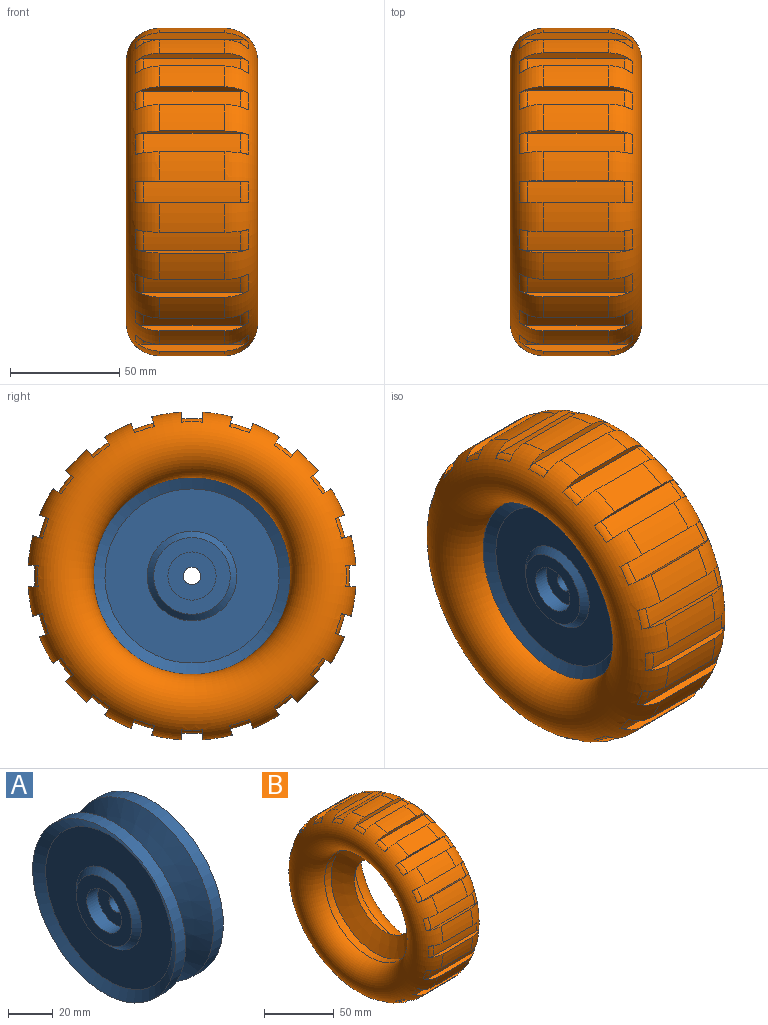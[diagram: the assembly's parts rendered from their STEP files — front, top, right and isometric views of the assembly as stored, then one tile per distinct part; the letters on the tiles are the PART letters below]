
ASSEMBLY  parts=2 mates=1
PART A: 17 faces, bbox 30x90x90 mm
  f0: plane 35x35mm, normal (-1,0,0), area 582mm2, adj f1,f16
  f1: cylinder r=11mm len=22mm, axis (-1,0,0), area 483.8mm2, adj f0,f2
  f2: plane 22x22mm, normal (-1,0,0), area 329.9mm2, adj f1,f3
  f3: cylinder r=4mm len=16mm, axis (-1,0,0), area 402.1mm2, adj f2,f4
  f4: plane 22x22mm, normal (1,0,0), area 329.9mm2, adj f3,f5
  f5: cylinder r=11mm len=22mm, axis (-1,0,0), area 483.8mm2, adj f4,f6
  f6: plane 35x35mm, normal (1,0,0), area 582mm2, adj f5,f15
  f7: plane 79.61x79.61mm, normal (1,0,0), area 3657.1mm2, adj f8,f15
  f8: cone r=39.8mm half-angle=60deg, axis (1,0,0), area 1598.5mm2, adj f7,f9
  f9: cylinder r=45mm len=90mm, axis (-1,0,0), area 1792.5mm2, adj f8,f10
  f10: cone r=45mm half-angle=60deg, axis (1,0,0), area 4081mm2, adj f9,f11
  f11: cone r=30mm half-angle=60deg, axis (-1,0,0), area 4081mm2, adj f10,f12
  f12: cylinder r=45mm len=90mm, axis (-1,0,0), area 1792.5mm2, adj f11,f13
  f13: cone r=39.8mm half-angle=60deg, axis (-1,0,0), area 1598.5mm2, adj f12,f14
  f14: plane 79.61x79.61mm, normal (-1,0,0), area 3657.1mm2, adj f13,f16
  f15: cone r=20.5mm half-angle=45deg, axis (-1,0,0), area 506.5mm2, adj f6,f7
  f16: cone r=17.5mm half-angle=45deg, axis (1,0,0), area 506.5mm2, adj f0,f14
PART B: 126 faces, bbox 60x162.4x162.4 mm
  f0: cylinder r=75mm len=30mm, axis (-1,0,0), area 406.6mm2, adj f20,f25,f28,f122
  f1: cylinder r=75mm len=30mm, axis (-1,0,0), area 406.6mm2, adj f20,f25,f117,f123
  f2: cylinder r=75mm len=30mm, axis (-1,0,0), area 406.6mm2, adj f20,f25,f112,f118
  f3: cylinder r=75mm len=30mm, axis (-1,0,0), area 406.6mm2, adj f20,f25,f107,f113
  f4: cylinder r=75mm len=30mm, axis (-1,0,0), area 406.6mm2, adj f20,f25,f102,f108
  f5: cylinder r=75mm len=30mm, axis (-1,0,0), area 406.6mm2, adj f20,f25,f97,f103
  f6: cylinder r=75mm len=30mm, axis (-1,0,0), area 406.6mm2, adj f20,f25,f92,f98
  f7: cylinder r=75mm len=30mm, axis (-1,0,0), area 406.6mm2, adj f20,f25,f87,f93
  f8: cylinder r=75mm len=30mm, axis (-1,0,0), area 406.6mm2, adj f20,f25,f82,f88
  f9: cylinder r=75mm len=30mm, axis (-1,0,0), area 406.6mm2, adj f20,f25,f77,f83
  f10: cylinder r=75mm len=30mm, axis (-1,0,0), area 406.6mm2, adj f20,f25,f72,f78
  f11: cylinder r=75mm len=30mm, axis (-1,0,0), area 406.6mm2, adj f20,f25,f67,f73
  f12: cylinder r=75mm len=30mm, axis (-1,0,0), area 406.6mm2, adj f20,f25,f62,f68
  f13: cylinder r=75mm len=30mm, axis (-1,0,0), area 406.6mm2, adj f20,f25,f57,f63
  f14: cylinder r=75mm len=30mm, axis (-1,0,0), area 406.6mm2, adj f20,f25,f52,f58
  f15: cylinder r=75mm len=30mm, axis (-1,0,0), area 406.6mm2, adj f20,f25,f47,f53
  f16: cylinder r=75mm len=30mm, axis (-1,0,0), area 406.6mm2, adj f20,f25,f42,f48
  f17: cylinder r=75mm len=30mm, axis (-1,0,0), area 406.6mm2, adj f20,f25,f37,f43
  f18: cylinder r=75mm len=30mm, axis (-1,0,0), area 406.6mm2, adj f20,f25,f32,f38
  f19: cylinder r=75mm len=30mm, axis (-1,0,0), area 406.6mm2, adj f20,f25,f27,f33
  f20: torus R=60mm, axis (-1,0,0), area 15426.1mm2, adj f0,f1,f2,f3,f4,f5,f6,f7
  f21: cylinder r=45mm len=90mm, axis (-1,0,0), area 1792.5mm2, adj f20,f22
  f22: cone r=30mm half-angle=60deg, axis (-1,0,0), area 4081mm2, adj f21,f23
  f23: cone r=45mm half-angle=60deg, axis (1,0,0), area 4081mm2, adj f22,f24
  f24: cylinder r=45mm len=90mm, axis (-1,0,0), area 1792.5mm2, adj f23,f25
  f25: torus R=60mm, axis (-1,0,0), area 15426.1mm2, adj f0,f1,f2,f3,f4,f5,f6,f7
  f26: cylinder r=72mm len=44.28mm, axis (1,0,0), area 425.4mm2, adj f27,f28,f29,f30
  f27: plane 51.42x4.49mm, normal (0,-1,0.07), area 127.7mm2, adj f19,f20,f25,f26,f29,f30
  f28: plane 51.42x4.49mm, normal (0,1,0.07), area 127.7mm2, adj f0,f20,f25,f26,f29,f30
  f29: torus R=67mm, axis (1,0,0), area 37.9mm2, adj f20,f26,f27,f28
  f30: torus R=67mm, axis (-1,0,0), area 37.9mm2, adj f25,f26,f27,f28
  f31: cylinder r=72mm len=44.28mm, axis (1,0,0), area 425.4mm2, adj f32,f33,f34,f35
  f32: plane 51.42x4.18mm, normal (0,-0.93,0.37), area 127.7mm2, adj f18,f20,f25,f31,f34,f35
  f33: plane 51.42x4.36mm, normal (0,0.97,-0.24), area 127.7mm2, adj f19,f20,f25,f31,f34,f35
  f34: torus R=67mm, axis (1,0,0), area 37.9mm2, adj f20,f31,f32,f33
  f35: torus R=67mm, axis (-1,0,0), area 37.9mm2, adj f25,f31,f32,f33
  f36: cylinder r=72mm len=44.28mm, axis (1,0,0), area 425.4mm2, adj f37,f38,f39,f40
  f37: plane 51.42x3.46mm, normal (0,-0.77,0.64), area 127.7mm2, adj f17,f20,f25,f36,f39,f40
  f38: plane 51.42x3.81mm, normal (0,0.85,-0.53), area 127.7mm2, adj f18,f20,f25,f36,f39,f40
  f39: torus R=67mm, axis (1,0,0), area 37.9mm2, adj f20,f36,f37,f38
  f40: torus R=67mm, axis (-1,0,0), area 37.9mm2, adj f25,f36,f37,f38
  f41: cylinder r=72mm len=44.28mm, axis (1,0,0), area 425.4mm2, adj f42,f43,f44,f45
  f42: plane 51.42x3.81mm, normal (0,-0.53,0.85), area 127.7mm2, adj f16,f20,f25,f41,f44,f45
  f43: plane 51.42x3.46mm, normal (0,0.64,-0.77), area 127.7mm2, adj f17,f20,f25,f41,f44,f45
  f44: torus R=67mm, axis (1,0,0), area 37.9mm2, adj f20,f41,f42,f43
  f45: torus R=67mm, axis (-1,0,0), area 37.9mm2, adj f25,f41,f42,f43
  f46: cylinder r=72mm len=44.28mm, axis (1,0,0), area 425.4mm2, adj f47,f48,f49,f50
  f47: plane 51.42x4.36mm, normal (0,-0.24,0.97), area 127.7mm2, adj f15,f20,f25,f46,f49,f50
  f48: plane 51.42x4.18mm, normal (0,0.37,-0.93), area 127.7mm2, adj f16,f20,f25,f46,f49,f50
  f49: torus R=67mm, axis (1,0,0), area 37.9mm2, adj f20,f46,f47,f48
  f50: torus R=67mm, axis (-1,0,0), area 37.9mm2, adj f25,f46,f47,f48
  f51: cylinder r=72mm len=44.28mm, axis (1,0,0), area 425.4mm2, adj f52,f53,f54,f55
  f52: plane 51.42x4.49mm, normal (0,0.07,1), area 127.7mm2, adj f14,f20,f25,f51,f54,f55
  f53: plane 51.42x4.49mm, normal (0,0.07,-1), area 127.7mm2, adj f15,f20,f25,f51,f54,f55
  f54: torus R=67mm, axis (1,0,0), area 37.9mm2, adj f20,f51,f52,f53
  f55: torus R=67mm, axis (-1,0,0), area 37.9mm2, adj f25,f51,f52,f53
  f56: cylinder r=72mm len=44.28mm, axis (1,0,0), area 425.4mm2, adj f57,f58,f59,f60
  f57: plane 51.42x4.18mm, normal (0,0.37,0.93), area 127.7mm2, adj f13,f20,f25,f56,f59,f60
  f58: plane 51.42x4.36mm, normal (0,-0.24,-0.97), area 127.7mm2, adj f14,f20,f25,f56,f59,f60
  f59: torus R=67mm, axis (1,0,0), area 37.9mm2, adj f20,f56,f57,f58
  f60: torus R=67mm, axis (-1,0,0), area 37.9mm2, adj f25,f56,f57,f58
  f61: cylinder r=72mm len=44.28mm, axis (1,0,0), area 425.4mm2, adj f62,f63,f64,f65
  f62: plane 51.42x3.46mm, normal (0,0.64,0.77), area 127.7mm2, adj f12,f20,f25,f61,f64,f65
  f63: plane 51.42x3.81mm, normal (0,-0.53,-0.85), area 127.7mm2, adj f13,f20,f25,f61,f64,f65
  f64: torus R=67mm, axis (1,0,0), area 37.9mm2, adj f20,f61,f62,f63
  f65: torus R=67mm, axis (-1,0,0), area 37.9mm2, adj f25,f61,f62,f63
  f66: cylinder r=72mm len=44.28mm, axis (1,0,0), area 425.4mm2, adj f67,f68,f69,f70
  f67: plane 51.42x3.81mm, normal (0,0.85,0.53), area 127.7mm2, adj f11,f20,f25,f66,f69,f70
  f68: plane 51.42x3.46mm, normal (0,-0.77,-0.64), area 127.7mm2, adj f12,f20,f25,f66,f69,f70
  f69: torus R=67mm, axis (1,0,0), area 37.9mm2, adj f20,f66,f67,f68
  f70: torus R=67mm, axis (-1,0,0), area 37.9mm2, adj f25,f66,f67,f68
  f71: cylinder r=72mm len=44.28mm, axis (1,0,0), area 425.4mm2, adj f72,f73,f74,f75
  f72: plane 51.42x4.36mm, normal (0,0.97,0.24), area 127.7mm2, adj f10,f20,f25,f71,f74,f75
  f73: plane 51.42x4.18mm, normal (0,-0.93,-0.37), area 127.7mm2, adj f11,f20,f25,f71,f74,f75
  f74: torus R=67mm, axis (1,0,0), area 37.9mm2, adj f20,f71,f72,f73
  f75: torus R=67mm, axis (-1,0,0), area 37.9mm2, adj f25,f71,f72,f73
  f76: cylinder r=72mm len=44.28mm, axis (1,0,0), area 425.4mm2, adj f77,f78,f79,f80
  f77: plane 51.42x4.49mm, normal (0,1,-0.07), area 127.7mm2, adj f9,f20,f25,f76,f79,f80
  f78: plane 51.42x4.49mm, normal (0,-1,-0.07), area 127.7mm2, adj f10,f20,f25,f76,f79,f80
  f79: torus R=67mm, axis (1,0,0), area 37.9mm2, adj f20,f76,f77,f78
  f80: torus R=67mm, axis (-1,0,0), area 37.9mm2, adj f25,f76,f77,f78
  f81: cylinder r=72mm len=44.28mm, axis (1,0,0), area 425.4mm2, adj f82,f83,f84,f85
  f82: plane 51.42x4.18mm, normal (0,0.93,-0.37), area 127.7mm2, adj f8,f20,f25,f81,f84,f85
  f83: plane 51.42x4.36mm, normal (0,-0.97,0.24), area 127.7mm2, adj f9,f20,f25,f81,f84,f85
  f84: torus R=67mm, axis (1,0,0), area 37.9mm2, adj f20,f81,f82,f83
  f85: torus R=67mm, axis (-1,0,0), area 37.9mm2, adj f25,f81,f82,f83
  f86: cylinder r=72mm len=44.28mm, axis (1,0,0), area 425.4mm2, adj f87,f88,f89,f90
  f87: plane 51.42x3.46mm, normal (0,0.77,-0.64), area 127.7mm2, adj f7,f20,f25,f86,f89,f90
  f88: plane 51.42x3.81mm, normal (0,-0.85,0.53), area 127.7mm2, adj f8,f20,f25,f86,f89,f90
  f89: torus R=67mm, axis (1,0,0), area 37.9mm2, adj f20,f86,f87,f88
  f90: torus R=67mm, axis (-1,0,0), area 37.9mm2, adj f25,f86,f87,f88
  f91: cylinder r=72mm len=44.28mm, axis (1,0,0), area 425.4mm2, adj f92,f93,f94,f95
  f92: plane 51.42x3.81mm, normal (0,0.53,-0.85), area 127.7mm2, adj f6,f20,f25,f91,f94,f95
  f93: plane 51.42x3.46mm, normal (0,-0.64,0.77), area 127.7mm2, adj f7,f20,f25,f91,f94,f95
  f94: torus R=67mm, axis (1,0,0), area 37.9mm2, adj f20,f91,f92,f93
  f95: torus R=67mm, axis (-1,0,0), area 37.9mm2, adj f25,f91,f92,f93
  f96: cylinder r=72mm len=44.28mm, axis (1,0,0), area 425.4mm2, adj f97,f98,f99,f100
  f97: plane 51.42x4.36mm, normal (0,0.24,-0.97), area 127.7mm2, adj f5,f20,f25,f96,f99,f100
  f98: plane 51.42x4.18mm, normal (0,-0.37,0.93), area 127.7mm2, adj f6,f20,f25,f96,f99,f100
  f99: torus R=67mm, axis (1,0,0), area 37.9mm2, adj f20,f96,f97,f98
  f100: torus R=67mm, axis (-1,0,0), area 37.9mm2, adj f25,f96,f97,f98
  f101: cylinder r=72mm len=44.28mm, axis (1,0,0), area 425.4mm2, adj f102,f103,f104,f105
  f102: plane 51.42x4.49mm, normal (0,-0.07,-1), area 127.7mm2, adj f4,f20,f25,f101,f104,f105
  f103: plane 51.42x4.49mm, normal (0,-0.07,1), area 127.7mm2, adj f5,f20,f25,f101,f104,f105
  f104: torus R=67mm, axis (1,0,0), area 37.9mm2, adj f20,f101,f102,f103
  f105: torus R=67mm, axis (-1,0,0), area 37.9mm2, adj f25,f101,f102,f103
  f106: cylinder r=72mm len=44.28mm, axis (1,0,0), area 425.4mm2, adj f107,f108,f109,f110
  f107: plane 51.42x4.18mm, normal (0,-0.37,-0.93), area 127.7mm2, adj f3,f20,f25,f106,f109,f110
  f108: plane 51.42x4.36mm, normal (0,0.24,0.97), area 127.7mm2, adj f4,f20,f25,f106,f109,f110
  f109: torus R=67mm, axis (1,0,0), area 37.9mm2, adj f20,f106,f107,f108
  f110: torus R=67mm, axis (-1,0,0), area 37.9mm2, adj f25,f106,f107,f108
  f111: cylinder r=72mm len=44.28mm, axis (1,0,0), area 425.4mm2, adj f112,f113,f114,f115
  f112: plane 51.42x3.46mm, normal (0,-0.64,-0.77), area 127.7mm2, adj f2,f20,f25,f111,f114,f115
  f113: plane 51.42x3.81mm, normal (0,0.53,0.85), area 127.7mm2, adj f3,f20,f25,f111,f114,f115
  f114: torus R=67mm, axis (1,0,0), area 37.9mm2, adj f20,f111,f112,f113
  f115: torus R=67mm, axis (-1,0,0), area 37.9mm2, adj f25,f111,f112,f113
  f116: cylinder r=72mm len=44.28mm, axis (1,0,0), area 425.4mm2, adj f117,f118,f119,f120
  f117: plane 51.42x3.81mm, normal (0,-0.85,-0.53), area 127.7mm2, adj f1,f20,f25,f116,f119,f120
  f118: plane 51.42x3.46mm, normal (0,0.77,0.64), area 127.7mm2, adj f2,f20,f25,f116,f119,f120
  f119: torus R=67mm, axis (1,0,0), area 37.9mm2, adj f20,f116,f117,f118
  f120: torus R=67mm, axis (-1,0,0), area 37.9mm2, adj f25,f116,f117,f118
  f121: cylinder r=72mm len=44.28mm, axis (1,0,0), area 425.4mm2, adj f122,f123,f124,f125
  f122: plane 51.42x4.36mm, normal (0,-0.97,-0.24), area 127.7mm2, adj f0,f20,f25,f121,f124,f125
  f123: plane 51.42x4.18mm, normal (0,0.93,0.37), area 127.7mm2, adj f1,f20,f25,f121,f124,f125
  f124: torus R=67mm, axis (1,0,0), area 37.9mm2, adj f20,f121,f122,f123
  f125: torus R=67mm, axis (-1,0,0), area 37.9mm2, adj f25,f121,f122,f123
PLACE A at identity
PLACE B at identity
MATE fastened B.f0 <-> A.f1  axis (-1,0,0) through (0,0,0)mm
